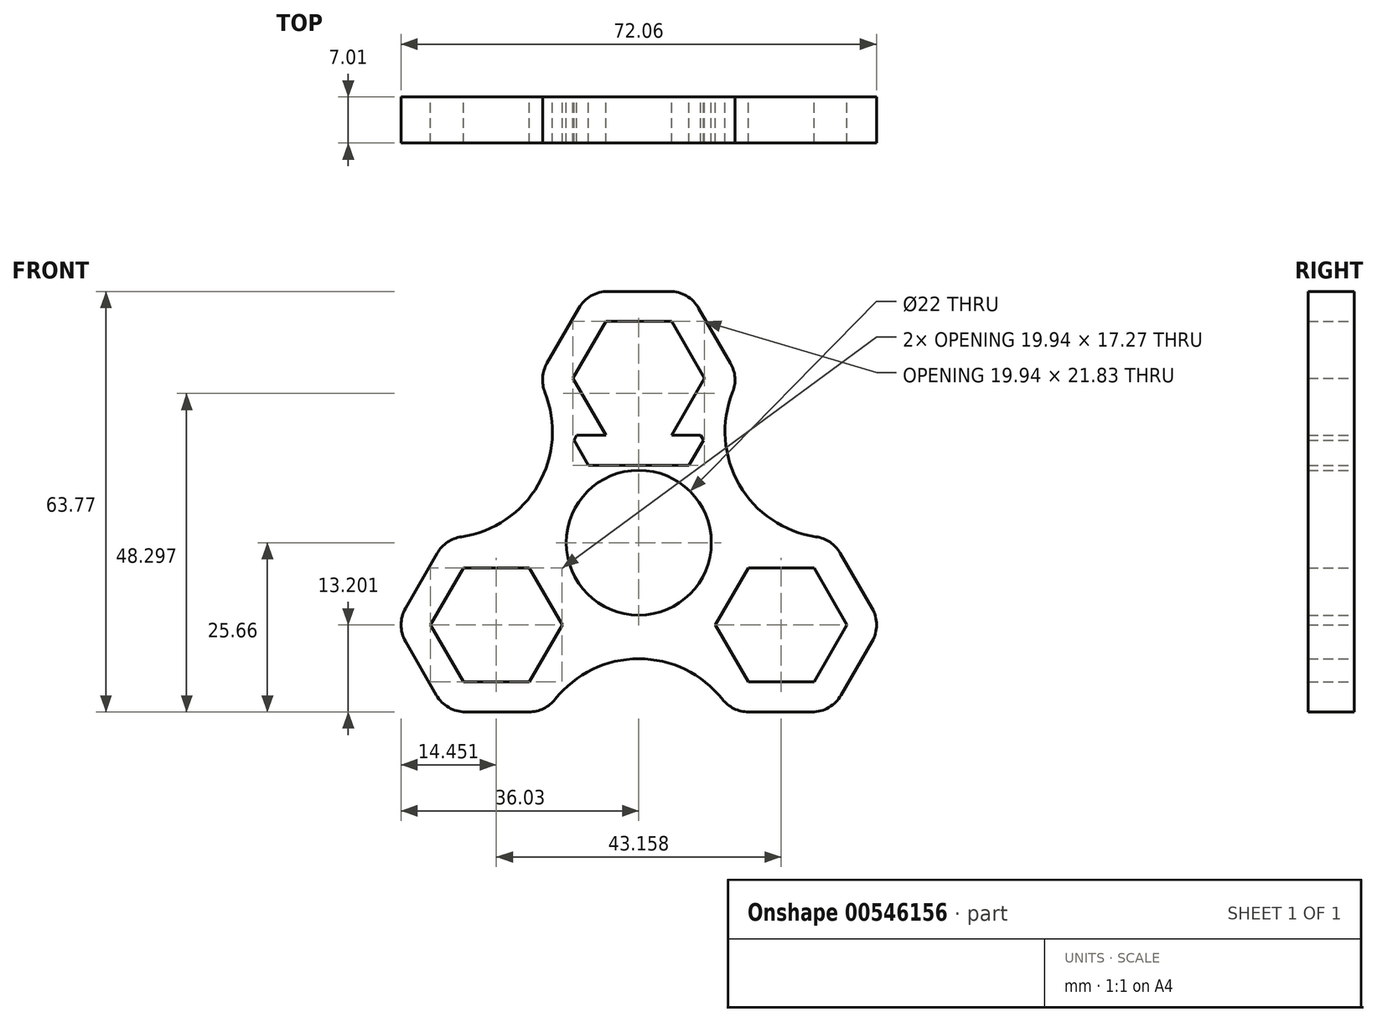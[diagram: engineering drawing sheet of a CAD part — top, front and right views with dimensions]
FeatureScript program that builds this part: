
annotation { "Feature Type Name" : "Feature", "Feature Type Description" : "" }
export const myFeature = defineFeature(function(context is Context, id is Id, definition is map)
    precondition{}
    {
        {
            var Q0;
            Q0=qCreatedBy(makeId("Front.planeOp"),FACE);
            var sketch = newSketch(context, id + "F0", { "sketchPlane" : qUnion([Q0])});
            skCircle(sketch, "E0", {"center": v(0, 0) * mm, "radius": 11 * mm});
            skCircle(sketch, "E1.cCircle", {"center": v(0, 0) * mm, "radius": 16.28 * mm, "construction": true});
            skLineSegment(sketch, "E1.0", {"start": v(-9.4, 16.28) * mm, "end": v(9.4, 16.28) * mm});
            skLineSegment(sketch, "E1.1", {"start": v(9.4, 16.28) * mm, "end": v(18.8, 0) * mm});
            skLineSegment(sketch, "E1.2", {"start": v(18.8, 0) * mm, "end": v(9.4, -16.28) * mm});
            skLineSegment(sketch, "E1.3", {"start": v(9.4, -16.28) * mm, "end": v(-9.4, -16.28) * mm});
            skLineSegment(sketch, "E1.4", {"start": v(-9.4, -16.28) * mm, "end": v(-18.8, 0) * mm});
            skLineSegment(sketch, "E1.5", {"start": v(-18.8, 0) * mm, "end": v(-9.4, 16.28) * mm});
            skPoint(sketch, "E2.0.midPoint", {"position": v(0, 11) * mm});
            skCircle(sketch, "E3.cCircle", {"center": v(0, 24.92) * mm, "radius": 8.64 * mm, "construction": true});
            skLineSegment(sketch, "E3.0", {"start": v(4.99, 16.28) * mm, "end": v(-4.99, 16.28) * mm});
            skLineSegment(sketch, "E3.1", {"start": v(-4.99, 16.28) * mm, "end": v(-9.97, 24.92) * mm});
            skLineSegment(sketch, "E3.2", {"start": v(-9.97, 24.92) * mm, "end": v(-4.99, 33.55) * mm});
            skLineSegment(sketch, "E3.3", {"start": v(-4.99, 33.55) * mm, "end": v(4.99, 33.55) * mm});
            skLineSegment(sketch, "E3.4", {"start": v(4.99, 33.55) * mm, "end": v(9.97, 24.92) * mm});
            skLineSegment(sketch, "E3.5", {"start": v(9.97, 24.92) * mm, "end": v(4.99, 16.28) * mm});
            skPoint(sketch, "E3.0.midPoint", {"position": v(0, 16.28) * mm});
            skCircle(sketch, "E4.cCircle", {"center": v(0, 24.92) * mm, "radius": 13.2 * mm, "construction": true});
            skPoint(sketch, "E4.cCircle.perimeterSnap0", {"position": v(0, 33.55) * mm});
            skLineSegment(sketch, "E4.0", {"start": v(-7.62, 38.11) * mm, "end": v(7.62, 38.11) * mm});
            skLineSegment(sketch, "E4.1", {"start": v(7.62, 38.11) * mm, "end": v(15.24, 24.92) * mm});
            skLineSegment(sketch, "E4.2", {"start": v(15.24, 24.92) * mm, "end": v(7.62, 11.72) * mm});
            skLineSegment(sketch, "E4.3", {"start": v(7.62, 11.72) * mm, "end": v(-7.62, 11.72) * mm});
            skLineSegment(sketch, "E4.4", {"start": v(-7.62, 11.72) * mm, "end": v(-15.24, 24.92) * mm});
            skLineSegment(sketch, "E4.5", {"start": v(-15.24, 24.92) * mm, "end": v(-7.62, 38.11) * mm});
            skPoint(sketch, "E4.0.midPoint", {"position": v(0, 38.11) * mm});
            skPoint(sketch, "E4.0.midPoint.positionSnap0", {"position": v(0, 33.55) * mm});
            skCircle(sketch, "E5.1.0", {"center": v(-21.58, -12.46) * mm, "radius": 13.2 * mm, "construction": true});
            skLineSegment(sketch, "E5.1.1", {"start": v(-16.6, -21.1) * mm, "end": v(-26.57, -21.1) * mm});
            skLineSegment(sketch, "E5.1.2", {"start": v(-26.57, -21.1) * mm, "end": v(-31.55, -12.46) * mm});
            skLineSegment(sketch, "E5.1.3", {"start": v(-31.55, -12.46) * mm, "end": v(-26.57, -3.82) * mm});
            skLineSegment(sketch, "E5.1.4", {"start": v(-26.57, -3.82) * mm, "end": v(-16.6, -3.82) * mm});
            skCircle(sketch, "E5.1.5", {"center": v(-21.58, -12.46) * mm, "radius": 8.64 * mm, "construction": true});
            skLineSegment(sketch, "E5.1.6", {"start": v(-11.6, -12.46) * mm, "end": v(-16.6, -21.1) * mm});
            skLineSegment(sketch, "E5.1.7", {"start": v(-13.96, 0.74) * mm, "end": v(-6.34, -12.46) * mm});
            skLineSegment(sketch, "E5.1.8", {"start": v(-6.34, -12.46) * mm, "end": v(-13.96, -25.66) * mm});
            skLineSegment(sketch, "E5.1.9", {"start": v(-29.2, 0.74) * mm, "end": v(-13.96, 0.74) * mm});
            skLineSegment(sketch, "E5.1.10", {"start": v(-36.82, -12.46) * mm, "end": v(-29.2, 0.74) * mm});
            skLineSegment(sketch, "E5.1.11", {"start": v(-29.2, -25.66) * mm, "end": v(-36.82, -12.46) * mm});
            skLineSegment(sketch, "E5.1.12", {"start": v(-13.96, -25.66) * mm, "end": v(-29.2, -25.66) * mm});
            skCircle(sketch, "E5.2.0", {"center": v(21.58, -12.46) * mm, "radius": 13.2 * mm, "construction": true});
            skLineSegment(sketch, "E5.2.1", {"start": v(26.57, -3.82) * mm, "end": v(31.55, -12.46) * mm});
            skLineSegment(sketch, "E5.2.2", {"start": v(31.55, -12.46) * mm, "end": v(26.57, -21.1) * mm});
            skLineSegment(sketch, "E5.2.3", {"start": v(26.57, -21.1) * mm, "end": v(16.6, -21.1) * mm});
            skLineSegment(sketch, "E5.2.4", {"start": v(16.6, -21.1) * mm, "end": v(11.6, -12.46) * mm});
            skCircle(sketch, "E5.2.5", {"center": v(21.58, -12.46) * mm, "radius": 8.64 * mm, "construction": true});
            skLineSegment(sketch, "E5.2.6", {"start": v(16.6, -3.82) * mm, "end": v(26.57, -3.82) * mm});
            skLineSegment(sketch, "E5.2.7", {"start": v(6.34, -12.46) * mm, "end": v(13.96, 0.74) * mm});
            skLineSegment(sketch, "E5.2.8", {"start": v(13.96, 0.74) * mm, "end": v(29.2, 0.74) * mm});
            skLineSegment(sketch, "E5.2.9", {"start": v(13.96, -25.66) * mm, "end": v(6.34, -12.46) * mm});
            skLineSegment(sketch, "E5.2.10", {"start": v(29.2, -25.66) * mm, "end": v(13.96, -25.66) * mm});
            skLineSegment(sketch, "E5.2.11", {"start": v(36.82, -12.46) * mm, "end": v(29.2, -25.66) * mm});
            skLineSegment(sketch, "E5.2.12", {"start": v(29.2, 0.74) * mm, "end": v(36.82, -12.46) * mm});
            skArc(sketch, "E6", {"start": v(15.24, 24.92) * mm, "mid": v(15.24, 8.8) * mm, "end": v(29.2, 0.74) * mm});
            skArc(sketch, "E7", {"start": v(13.96, -25.66) * mm, "mid": v(0, -17.6) * mm, "end": v(-13.96, -25.66) * mm});
            skArc(sketch, "E8", {"start": v(-29.2, 0.74) * mm, "mid": v(-15.24, 8.8) * mm, "end": v(-15.24, 24.92) * mm});
            skSolve(sketch);
        }
        {
            var Q0;
            Q0 = qSketchRegion(id + "F0", true);
            var Q1;
            Q1=makeQuery(id+"F0.imprint","IMPRINT",FACE,{"disambiguationData":[TD([[makeQuery(id+"F0.imprint","IMPRINT",EDGE,{"derivedFrom":sQuery(id+"F0.wireOp",EDGE,"E0")}),-1.0]])]});
            var Q2;
            {var subQ10=sQuery(id+"F0.wireOp",EDGE,"E3.0");Q2=makeQuery(id+"F0.imprint","IMPRINT",FACE,{"disambiguationData":[TD([[makeQuery(id+"F0.imprint","IMPRINT",EDGE,{"derivedFrom":subQ10}),1.0]])]});}
            var Q3;
            {var subQ6=sQuery(id+"F0.wireOp",EDGE,"E5.2.7");Q3=makeQuery(id+"F0.imprint","IMPRINT",FACE,{"disambiguationData":[TD([[makeQuery(id+"F0.imprint","IMPRINT",EDGE,{"derivedFrom":subQ6}),-1.0]])]});}
            var Q4;
            {var subQ11=sQuery(id+"F0.wireOp",EDGE,"E5.1.7");Q4=makeQuery(id+"F0.imprint","IMPRINT",FACE,{"disambiguationData":[TD([[makeQuery(id+"F0.imprint","IMPRINT",EDGE,{"derivedFrom":subQ11}),-1.0]])]});}
            extrude(context, id + "F1", {"entities" : qUnion([Q0, Q1, Q2, Q3, Q4]), "depth" : 7 * mm, "offsetDistance" : 25.4 * mm});
        }
        {
            var Q0;
            Q0=makeQuery(id+"F1.opExtrude","SWEPT_EDGE",EDGE,{"disambiguationData":[OSD([sQuery(id+"F0.wireOp",EDGE,"E4.4"),sQuery(id+"F0.wireOp",EDGE,"E4.5"),sQuery(id+"F0.wireOp",EDGE,"E8")])]});
            var Q1;
            Q1=makeQuery(id+"F1.opExtrude","SWEPT_EDGE",EDGE,{"disambiguationData":[OSD([sQuery(id+"F0.wireOp",EDGE,"E4.0"),sQuery(id+"F0.wireOp",EDGE,"E4.5")])]});
            var Q2;
            Q2=makeQuery(id+"F1.opExtrude","SWEPT_EDGE",EDGE,{"disambiguationData":[OSD([sQuery(id+"F0.wireOp",EDGE,"E4.0"),sQuery(id+"F0.wireOp",EDGE,"E4.1")])]});
            var Q3;
            Q3=makeQuery(id+"F1.opExtrude","SWEPT_EDGE",EDGE,{"disambiguationData":[OSD([sQuery(id+"F0.wireOp",EDGE,"E4.1"),sQuery(id+"F0.wireOp",EDGE,"E4.2"),sQuery(id+"F0.wireOp",EDGE,"E6")])]});
            var Q4;
            Q4=makeQuery(id+"F1.opExtrude","SWEPT_EDGE",EDGE,{"disambiguationData":[OSD([sQuery(id+"F0.wireOp",EDGE,"E5.2.8"),sQuery(id+"F0.wireOp",EDGE,"E5.2.12"),sQuery(id+"F0.wireOp",EDGE,"E6")])]});
            var Q5;
            Q5=makeQuery(id+"F1.opExtrude","SWEPT_EDGE",EDGE,{"disambiguationData":[OSD([sQuery(id+"F0.wireOp",EDGE,"E5.2.11"),sQuery(id+"F0.wireOp",EDGE,"E5.2.12")])]});
            var Q6;
            Q6=makeQuery(id+"F1.opExtrude","SWEPT_EDGE",EDGE,{"disambiguationData":[OSD([sQuery(id+"F0.wireOp",EDGE,"E5.2.10"),sQuery(id+"F0.wireOp",EDGE,"E5.2.11")])]});
            var Q7;
            Q7=makeQuery(id+"F1.opExtrude","SWEPT_EDGE",EDGE,{"disambiguationData":[OSD([sQuery(id+"F0.wireOp",EDGE,"E5.2.9"),sQuery(id+"F0.wireOp",EDGE,"E5.2.10"),sQuery(id+"F0.wireOp",EDGE,"E7")])]});
            var Q8;
            Q8=makeQuery(id+"F1.opExtrude","SWEPT_EDGE",EDGE,{"disambiguationData":[OSD([sQuery(id+"F0.wireOp",EDGE,"E5.1.10"),sQuery(id+"F0.wireOp",EDGE,"E5.1.11")])]});
            var Q9;
            Q9=makeQuery(id+"F1.opExtrude","SWEPT_EDGE",EDGE,{"disambiguationData":[OSD([sQuery(id+"F0.wireOp",EDGE,"E5.1.11"),sQuery(id+"F0.wireOp",EDGE,"E5.1.12")])]});
            var Q10;
            Q10=makeQuery(id+"F1.opExtrude","SWEPT_EDGE",EDGE,{"disambiguationData":[OSD([sQuery(id+"F0.wireOp",EDGE,"E5.1.8"),sQuery(id+"F0.wireOp",EDGE,"E5.1.12"),sQuery(id+"F0.wireOp",EDGE,"E7")])]});
            var Q11;
            Q11=makeQuery(id+"F1.opExtrude","SWEPT_EDGE",EDGE,{"disambiguationData":[OSD([sQuery(id+"F0.wireOp",EDGE,"E5.1.9"),sQuery(id+"F0.wireOp",EDGE,"E5.1.10"),sQuery(id+"F0.wireOp",EDGE,"E8")])]});
            fillet(context, id + "F2", {"entities" : qUnion([Q0, Q1, Q2, Q3, Q4, Q5, Q6, Q7, Q8, Q9, Q10, Q11]), "radius" : 5.08 * mm, "tangentPropagation" : true, "allowEdgeOverflow" : false});
        }
    });
